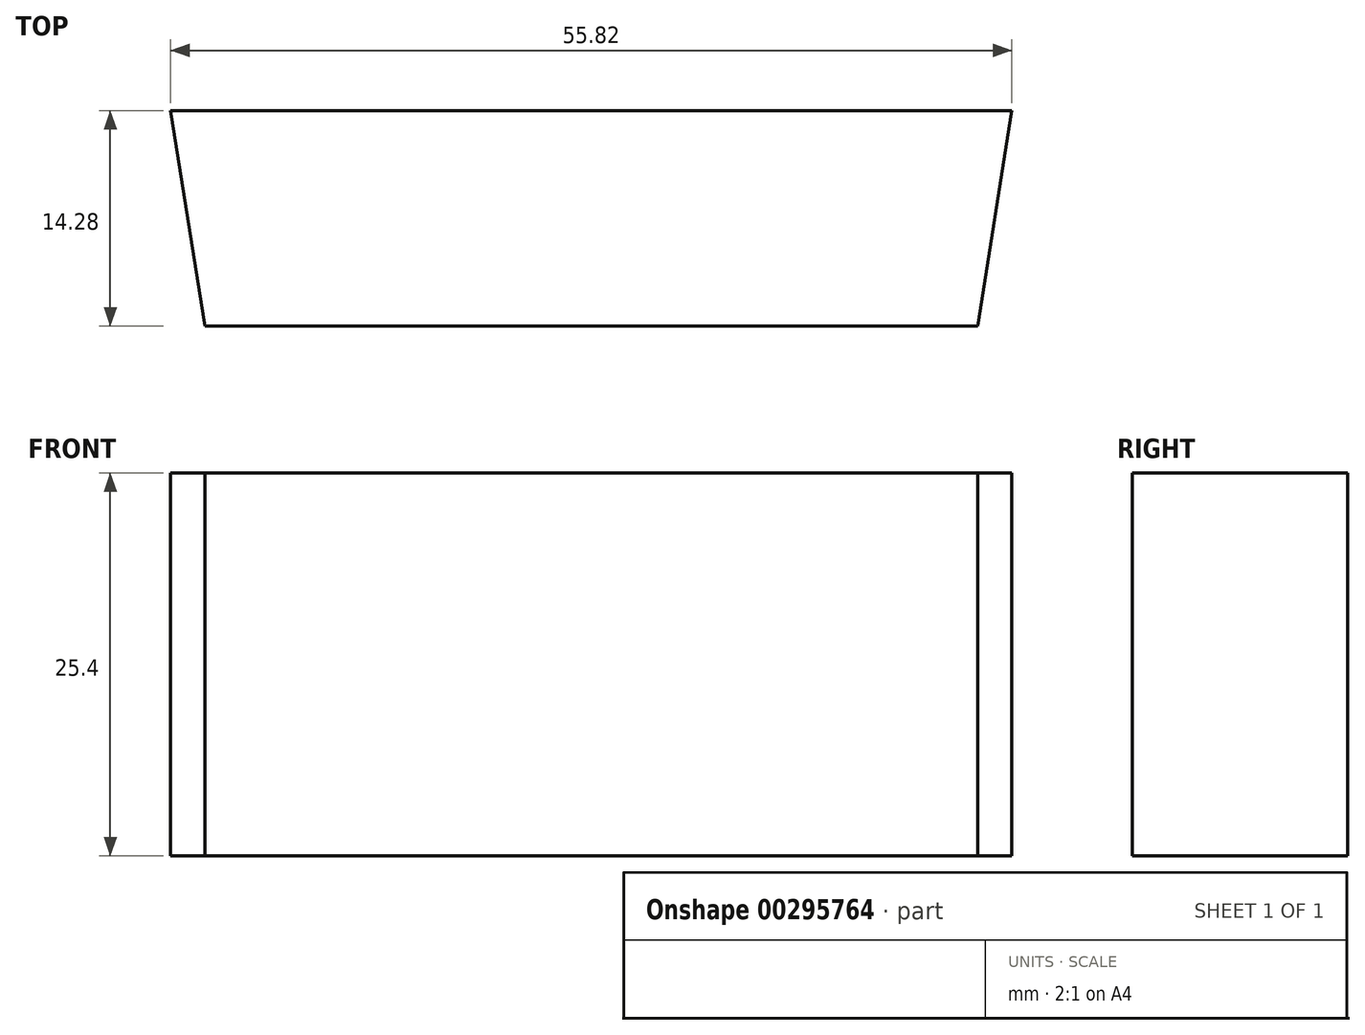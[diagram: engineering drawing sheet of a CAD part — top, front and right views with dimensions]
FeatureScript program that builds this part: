
annotation { "Feature Type Name" : "Feature", "Feature Type Description" : "" }
export const myFeature = defineFeature(function(context is Context, id is Id, definition is map)
    precondition{}
    {
        {
            var Q0;
            Q0=qCreatedBy(makeId("Top.planeOp"),FACE);
            var sketch = newSketch(context, id + "F0", { "sketchPlane" : qUnion([Q0])});
            skLineSegment(sketch, "E0", {"start": v(-27.9, 176.21) * mm, "end": v(27.9, 176.21) * mm});
            skLineSegment(sketch, "E1", {"start": v(-27.9, 176.21) * mm, "end": v(0, 0) * mm, "construction": true});
            skLineSegment(sketch, "E2", {"start": v(0, 0) * mm, "end": v(27.9, 176.21) * mm, "construction": true});
            skLineSegment(sketch, "E3", {"start": v(-25.65, 161.93) * mm, "end": v(25.65, 161.93) * mm});
            skArc(sketch, "E4", {"start": v(25.65, 161.93) * mm, "mid": v(0, 163.94) * mm, "end": v(-25.65, 161.93) * mm, "construction": true});
            skArc(sketch, "E5", {"start": v(27.57, 174.04) * mm, "mid": v(0, 176.21) * mm, "end": v(-27.57, 174.04) * mm, "construction": true});
            skLineSegment(sketch, "E6", {"start": v(25.65, 161.93) * mm, "end": v(27.9, 176.21) * mm});
            skLineSegment(sketch, "E7", {"start": v(-25.65, 161.93) * mm, "end": v(-27.9, 176.21) * mm});
            skSolve(sketch);
        }
        {
            var Q0;
            Q0 = qSketchRegion(id + "F0", true);
            extrude(context, id + "F1", {"entities" : qUnion([Q0]), "depth" : 25.4 * mm});
        }
    });
